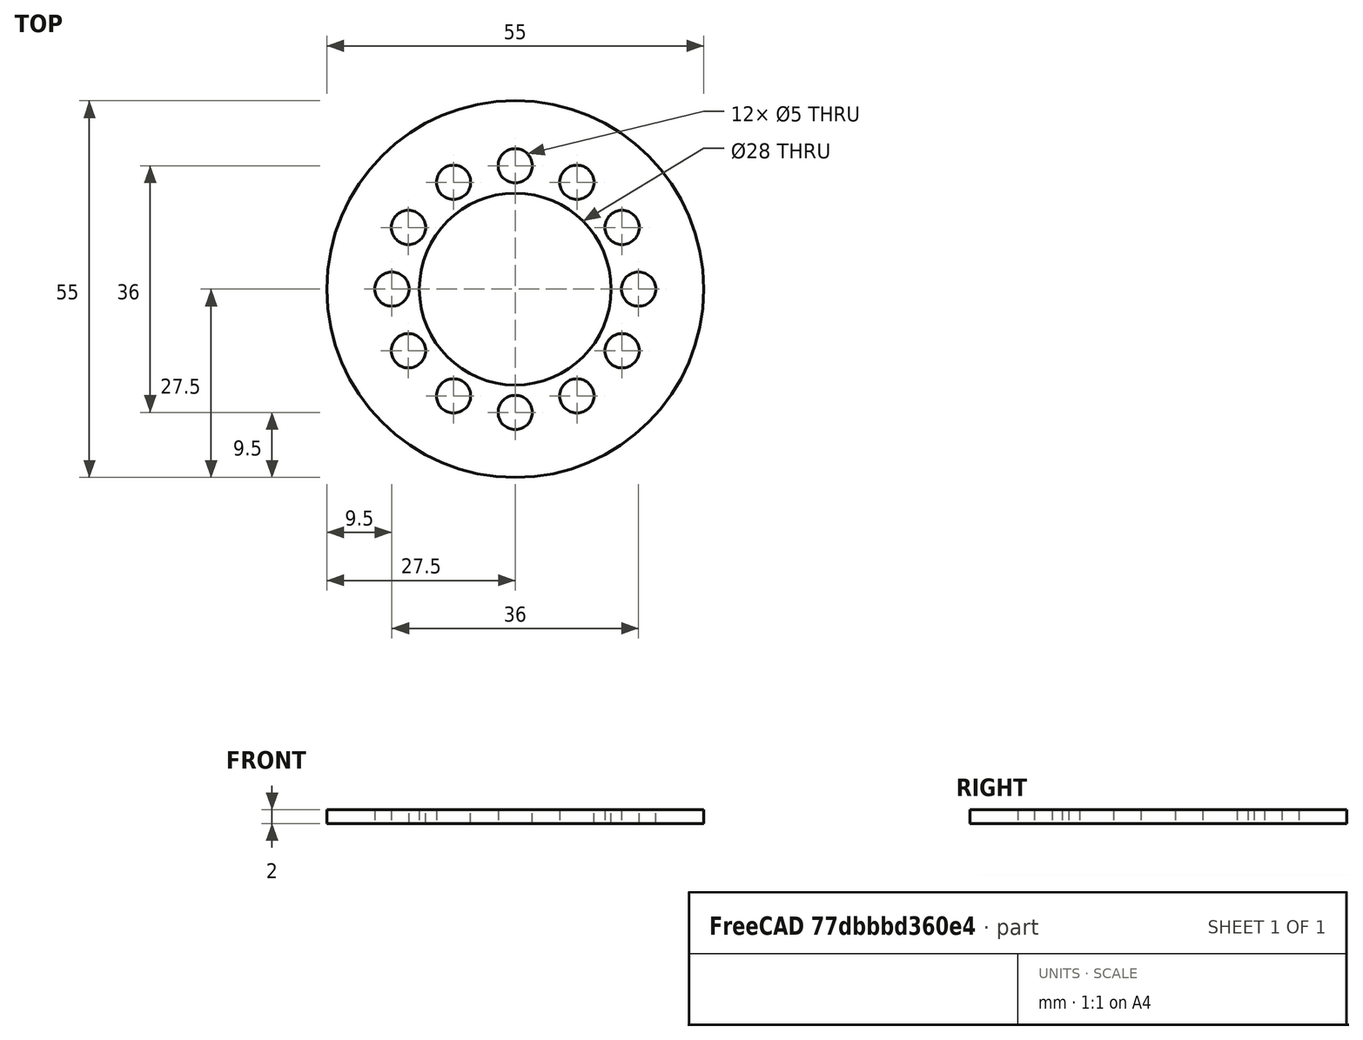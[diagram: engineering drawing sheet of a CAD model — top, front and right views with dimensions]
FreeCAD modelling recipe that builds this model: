
FCSTD DOCUMENT  (FreeCAD 0.19R24276 (Git))
Label: Bear_holder_for_d45_d75_substrate_2mm
License: All rights reserved
LicenseURL: http://en.wikipedia.org/wiki/All_rights_reserved
objects: Sketcher::SketchObject×1, PartDesign::Pad×1, PartDesign::Body×1
note: 4 computed .brp shape members not serialized (recipe doc carries the construction recipe); baked Part::Feature solids carry a one-line shape summary decoded from their .brp

FEATURE [Sketcher::SketchObject] Sketch
  FullyConstrained = false
  MapMode = 5
  Support = -> [XY_Plane]
  sketch-geometry (22):
    g0: Circle CenterX=0 CenterY=0 CenterZ=0 NormalX=0 NormalY=0 NormalZ=1 AngleXU=0 Radius=27.5
    g1: Circle CenterX=0 CenterY=0 CenterZ=0 NormalX=0 NormalY=0 NormalZ=1 AngleXU=0 Radius=14
    g2: LineSegment StartX=0 StartY=18 StartZ=0 EndX=-15.5885 EndY=-9 EndZ=0
    g3: LineSegment StartX=-15.5885 StartY=-9 StartZ=0 EndX=15.5885 EndY=-9 EndZ=0
    g4: LineSegment StartX=15.5885 StartY=-9 StartZ=0 EndX=0 EndY=18 EndZ=0
    g5: Circle CenterX=0 CenterY=0 CenterZ=0 NormalX=0 NormalY=0 NormalZ=1 AngleXU=0 Radius=18
    g6: Circle CenterX=0 CenterY=18 CenterZ=0 NormalX=0 NormalY=0 NormalZ=1 AngleXU=0 Radius=2.5
    g7: Circle CenterX=-15.5885 CenterY=-9 CenterZ=0 NormalX=0 NormalY=0 NormalZ=1 AngleXU=0 Radius=2.5
    g8: Circle CenterX=15.5885 CenterY=-9 CenterZ=0 NormalX=0 NormalY=0 NormalZ=1 AngleXU=0 Radius=2.5
    g9: LineSegment StartX=0 StartY=0 StartZ=0 EndX=-31.197 EndY=0 EndZ=0
    g10: Circle CenterX=0 CenterY=-18 CenterZ=0 NormalX=0 NormalY=0 NormalZ=1 AngleXU=0 Radius=2.5
    g11: Circle CenterX=-15.5885 CenterY=9 CenterZ=0 NormalX=0 NormalY=0 NormalZ=1 AngleXU=0 Radius=2.5
    g12: Circle CenterX=15.5885 CenterY=9 CenterZ=0 NormalX=0 NormalY=0 NormalZ=1 AngleXU=0 Radius=2.5
    g13: LineSegment StartX=0 StartY=0 StartZ=0 EndX=-9 EndY=15.5885 EndZ=0
    g14: Circle CenterX=-9 CenterY=15.5885 CenterZ=0 NormalX=0 NormalY=0 NormalZ=1 AngleXU=0 Radius=2.5
    g15: Circle CenterX=9 CenterY=-15.5885 CenterZ=0 NormalX=0 NormalY=0 NormalZ=1 AngleXU=0 Radius=2.5
    g16: Circle CenterX=9 CenterY=15.5885 CenterZ=0 NormalX=0 NormalY=0 NormalZ=1 AngleXU=0 Radius=2.5
    g17: LineSegment StartX=0 StartY=0 StartZ=0 EndX=0 EndY=-24.2336 EndZ=0
    g18: Circle CenterX=-9 CenterY=-15.5885 CenterZ=0 NormalX=0 NormalY=0 NormalZ=1 AngleXU=0 Radius=2.5
    g19: LineSegment StartX=0 StartY=0 StartZ=0 EndX=18 EndY=0 EndZ=0
    g20: Circle CenterX=18 CenterY=0 CenterZ=0 NormalX=0 NormalY=0 NormalZ=1 AngleXU=0 Radius=2.5
    g21: Circle CenterX=-18 CenterY=0 CenterZ=0 NormalX=0 NormalY=0 NormalZ=1 AngleXU=0 Radius=2.5
  constraints (37):
    c: Coincident(g0,g-1)
    c: Diameter(g0) = 55
    c: Coincident(g1,g-1)
    c: Coincident(g2,g3)
    c: Coincident(g3,g4)
    c: Coincident(g4,g2)
    c: Equal(g2,g3)
    c: Equal(g2,g4)
    c: PointOnObject(g2,g5)
    c: PointOnObject(g3,g5)
    c: PointOnObject(g4,g5)
    c: Coincident(g5,g-1)
    c: PointOnObject(g4,g-2)
    c: Coincident(g6,g2)
    c: Coincident(g7,g2)
    c: Coincident(g8,g3)
    c: Diameter(g8) = 5
    c: Equal(g8,g7)
    c: Equal(g8,g6)
    c: Diameter(g5) = 36
    c: Diameter(g1) = 28
    c: Coincident(g9,g0)
    c: PointOnObject(g9,g-1)
    c: Diameter(g12) = 5
    c: Equal(g12,g11)
    c: Coincident(g13,g0)
    c: PointOnObject(g13,g5)
    c: Angle(g13,g9) = 1.0472
    c: Coincident(g14,g13)
    c: Equal(g11,g14)
    c: Coincident(g17,g0)
    c: PointOnObject(g17,g-2)
    c: Coincident(g19,g0)
    c: PointOnObject(g19,g5)
    c: Horizontal(g19)
    c: Coincident(g20,g19)
    c: Equal(g12,g20)
FEATURE [PartDesign::Pad] Pad  label="Pad_h2"
  Direction = (1,1,1)
  Length = 2
  Length2 = 100
  Profile = -> Sketch
  Type = 0
FEATURE [PartDesign::Body] Body
  Group = -> [Sketch,Pad]
  Origin = -> Origin
  Tip = -> Pad
